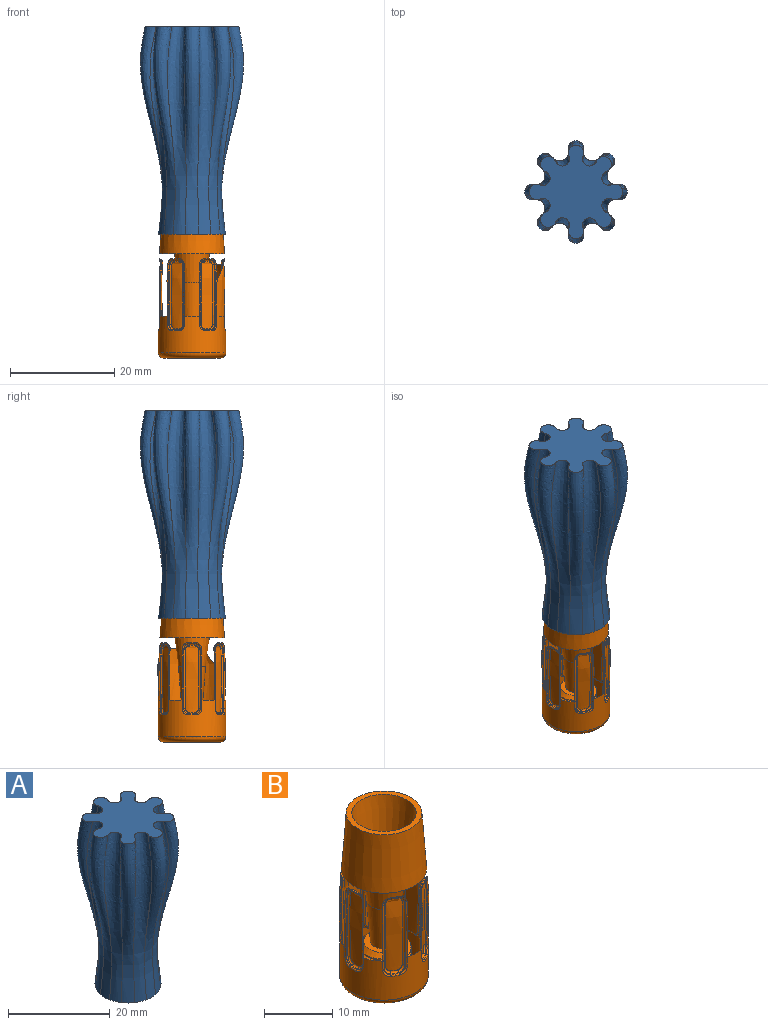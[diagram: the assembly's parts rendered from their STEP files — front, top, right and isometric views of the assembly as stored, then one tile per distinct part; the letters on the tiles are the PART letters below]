
ASSEMBLY  parts=2 mates=1
PART A: 18 faces, bbox 22.6x22.6x40 mm
  f0: plane 18x18mm, normal (0,0,1), area 169.5mm2, adj f2,f3,f4,f5,f6,f7,f8,f9
  f1: plane 13x13mm, normal (0,0,-1), area 132.7mm2, adj f2,f3,f4,f5,f6,f7,f8,f9
  f2: bspline ~40x5.48mm, area 140.4mm2, adj f0,f1,f3,f17
  f3: bspline ~40x5.84mm, area 146.5mm2, adj f0,f1,f2,f4
  f4: bspline ~40x5.48mm, area 140.4mm2, adj f0,f1,f3,f5
  f5: bspline ~40x6.75mm, area 146.5mm2, adj f0,f1,f4,f6
  f6: bspline ~40x5.48mm, area 140.4mm2, adj f0,f1,f5,f7
  f7: bspline ~40x5.84mm, area 146.5mm2, adj f0,f1,f6,f8
  f8: bspline ~40x5.48mm, area 140.4mm2, adj f0,f1,f7,f9
  f9: bspline ~40x6.75mm, area 146.5mm2, adj f0,f1,f8,f10
  f10: bspline ~40x5.48mm, area 140.4mm2, adj f0,f1,f9,f11
  f11: bspline ~40x5.84mm, area 146.5mm2, adj f0,f1,f10,f12
  f12: bspline ~40x5.48mm, area 140.4mm2, adj f0,f1,f11,f13
  f13: bspline ~40x6.75mm, area 146.5mm2, adj f0,f1,f12,f14
  f14: bspline ~40x5.48mm, area 140.4mm2, adj f0,f1,f13,f15
  f15: bspline ~40x5.84mm, area 146.5mm2, adj f0,f1,f14,f16
  f16: bspline ~40x5.48mm, area 140.4mm2, adj f0,f1,f15,f17
  f17: bspline ~40x6.75mm, area 146.5mm2, adj f0,f1,f2,f16
PART B: 180 faces, bbox 48.2x48.2x55.2 mm
  f0: plane 11x11mm, normal (0,0,-1), area 39.6mm2, adj f2,f177
  f1: cylinder r=6.5mm len=13mm, axis (0,0,-1), area 230.4mm2, adj f12,f37,f38,f39,f40,f41,f64,f65
  f2: cone r=4.2mm half-angle=45deg, axis (0,0,-1), area 18.5mm2, adj f0,f8,f9,f10,f11
  f3: plane 5.9x5.9mm, normal (0,0,-1), area 14.8mm2, adj f6,f179
  f4: plane 0.15x0.04mm, normal (-0.44,-0.9,0), area 0mm2, adj f5,f11
  f5: cylinder r=3.95mm len=3.48mm, axis (0,0,-1), area 0.3mm2, adj f4,f7,f10
  f6: cone r=2.95mm half-angle=45deg, axis (0,0,-1), area 19.2mm2, adj f3,f7,f9,f10
  f7: cone r=2.95mm half-angle=45deg, axis (0,0,-1), area 1.9mm2, adj f5,f6,f8,f10
  f8: bspline ~7.89x7.89mm, area 80.7mm2, adj f2,f7,f9,f11
  f9: cylinder r=3.43mm len=6.85mm, axis (0,0,1), area 30.4mm2, adj f2,f6,f8,f10
  f10: bspline ~7.9x7.89mm, area 80.6mm2, adj f2,f5,f6,f7,f9,f11
  f11: bspline ~9.25x8.32mm, area 24.8mm2, adj f2,f4,f8,f10
  f12: revolved ~13.14x13.13mm, area 207.3mm2, adj f1,f13,f32,f33,f34,f35,f36,f59
  f13: cone r=5.55mm half-angle=4deg, axis (0,0,-1), area 371.6mm2, adj f12,f14
  f14: plane 11.1x11.1mm, normal (0,0,1), area 27.4mm2, adj f13,f178
  f15: plane 1.29x0.23mm, normal (0,0,1), area 0.3mm2, adj f20,f23,f29,f41
  f16: cone r=8.65mm half-angle=83.7deg, axis (0,0,1), area 0.2mm2, adj f21,f22,f26,f32
  f17: plane 11.52x0.32mm, normal (0.26,0.97,0), area 1.5mm2, adj f22,f23,f25,f35,f37
  f18: plane 11.52x0.32mm, normal (0.26,-0.97,0), area 1.5mm2, adj f20,f21,f30,f36,f38
  f19: revolved ~12.85x2.53mm, area 31.3mm2, adj f24,f25,f26,f27,f28,f29,f30,f31
  f20: cylinder r=1mm len=1.04mm, axis (-0.97,-0.26,0), area 0.3mm2, adj f15,f18,f31,f40
  f21: bspline ~6.17x2.56mm, area 0.2mm2, adj f16,f18,f28,f34
  f22: bspline ~7.17x2.82mm, area 0.2mm2, adj f16,f17,f24,f33
  f23: cylinder r=1mm len=1.04mm, axis (0.97,-0.26,0), area 0.3mm2, adj f15,f17,f27,f39
  f24: bspline ~1.23x1.09mm, area 0.6mm2, adj f19,f22,f25,f26
  f25: bspline ~12.18x0.51mm, area 5.2mm2, adj f17,f19,f24,f27
  f26: torus R=5.99mm, axis (0,0,1), area 0.5mm2, adj f16,f19,f24,f28
  f27: bspline ~1.24x1.06mm, area 0.6mm2, adj f19,f23,f25,f29
  f28: bspline ~1.25x1.07mm, area 0.6mm2, adj f19,f21,f26,f30
  f29: torus R=6.09mm, axis (0,0,1), area 0.5mm2, adj f15,f19,f27,f31
  f30: bspline ~12.87x0.51mm, area 5.2mm2, adj f18,f19,f28,f31
  f31: bspline ~1.23x1.07mm, area 0.6mm2, adj f19,f20,f29,f30
  f32: torus R=6.11mm, axis (0,0,1), area 0.4mm2, adj f12,f16,f33,f34
  f33: bspline ~1.46x1.3mm, area 0.5mm2, adj f12,f22,f32,f35
  f34: bspline ~1.5x1.46mm, area 0.5mm2, adj f12,f21,f32,f36
  f35: bspline ~22.35x0.67mm, area 3.2mm2, adj f12,f17,f33,f37
  f36: bspline ~19.25x0.46mm, area 3.2mm2, adj f12,f18,f34,f38
  f37: cylinder r=0.2mm len=1.61mm, axis (0,0,-1), area 0.5mm2, adj f1,f17,f35,f39
  f38: cylinder r=0.2mm len=1.61mm, axis (0,0,-1), area 0.5mm2, adj f1,f18,f36,f40
  f39: bspline ~1.5x1.47mm, area 0.5mm2, adj f1,f23,f37,f41
  f40: bspline ~1.5x1.47mm, area 0.5mm2, adj f1,f20,f38,f41
  f41: torus R=6.3mm, axis (0,0,1), area 0.4mm2, adj f1,f15,f39,f40
  f42: plane 1.17x0.79mm, normal (0,0,1), area 0.3mm2, adj f47,f50,f56,f68
  f43: cone r=8.65mm half-angle=83.7deg, axis (0,0,1), area 0.2mm2, adj f48,f49,f53,f59
  f44: plane 11.52x0.32mm, normal (0.97,0.26,0), area 1.5mm2, adj f49,f50,f52,f62,f64
  f45: plane 11.52x0.23mm, normal (-0.71,-0.71,0), area 1.5mm2, adj f47,f48,f57,f63,f65
  f46: revolved ~12.85x2.27mm, area 31.3mm2, adj f51,f52,f53,f54,f55,f56,f57,f58
  f47: cylinder r=1mm len=1mm, axis (-0.71,0.71,0), area 0.3mm2, adj f42,f45,f58,f67
  f48: bspline ~5.1x5.03mm, area 0.2mm2, adj f43,f45,f55,f61
  f49: bspline ~7.28x2.81mm, area 0.2mm2, adj f43,f44,f51,f60
  f50: cylinder r=1mm len=1.04mm, axis (0.26,-0.97,0), area 0.3mm2, adj f42,f44,f54,f66
  f51: bspline ~1.23x1.03mm, area 0.6mm2, adj f46,f49,f52,f53
  f52: bspline ~12.87x0.6mm, area 5.2mm2, adj f44,f46,f51,f54
  f53: torus R=5.99mm, axis (0,0,1), area 0.5mm2, adj f43,f46,f51,f55
  f54: bspline ~1.23x1.06mm, area 0.6mm2, adj f46,f50,f52,f56
  f55: bspline ~1.19x1.07mm, area 0.6mm2, adj f46,f48,f53,f57
  f56: torus R=6.09mm, axis (0,0,1), area 0.5mm2, adj f42,f46,f54,f58
  f57: bspline ~12.87x0.58mm, area 5.2mm2, adj f45,f46,f55,f58
  f58: bspline ~1.23x1.12mm, area 0.6mm2, adj f46,f47,f56,f57
  f59: torus R=6.11mm, axis (0,0,1), area 0.4mm2, adj f12,f43,f60,f61
  f60: bspline ~1.46x1.2mm, area 0.5mm2, adj f12,f49,f59,f62
  f61: bspline ~1.46x1.28mm, area 0.5mm2, adj f12,f48,f59,f63
  f62: bspline ~22.35x0.71mm, area 3.2mm2, adj f12,f44,f60,f64
  f63: bspline ~19.25x0.48mm, area 3.2mm2, adj f12,f45,f61,f65
  f64: cylinder r=0.2mm len=1.61mm, axis (0,0,-1), area 0.5mm2, adj f1,f44,f62,f66
  f65: cylinder r=0.2mm len=1.61mm, axis (0,0,-1), area 0.5mm2, adj f1,f45,f63,f67
  f66: bspline ~1.47x1.43mm, area 0.5mm2, adj f1,f50,f64,f68
  f67: bspline ~1.47x1.24mm, area 0.5mm2, adj f1,f47,f65,f68
  f68: torus R=6.3mm, axis (0,0,1), area 0.4mm2, adj f1,f42,f66,f67
  f69: plane 1.17x0.79mm, normal (0,0,1), area 0.3mm2, adj f74,f77,f83,f95
  f70: cone r=8.65mm half-angle=83.7deg, axis (0,0,1), area 0.2mm2, adj f75,f76,f80,f86
  f71: plane 11.52x0.23mm, normal (0.71,-0.71,0), area 1.5mm2, adj f76,f77,f79,f89,f91
  f72: plane 11.52x0.32mm, normal (-0.97,0.26,0), area 1.5mm2, adj f74,f75,f84,f90,f92
  f73: revolved ~12.85x2.27mm, area 31.3mm2, adj f78,f79,f80,f81,f82,f83,f84,f85
  f74: cylinder r=1mm len=1.04mm, axis (0.26,0.97,0), area 0.3mm2, adj f69,f72,f85,f94
  f75: bspline ~6.28x2.54mm, area 0.2mm2, adj f70,f72,f82,f88
  f76: bspline ~5.83x5.76mm, area 0.2mm2, adj f70,f71,f78,f87
  f77: cylinder r=1mm len=1mm, axis (-0.71,-0.71,0), area 0.3mm2, adj f69,f71,f81,f93
  f78: bspline ~1.23x1.06mm, area 0.6mm2, adj f73,f76,f79,f80
  f79: bspline ~12.18x0.58mm, area 5.2mm2, adj f71,f73,f78,f81
  f80: torus R=5.99mm, axis (0,0,1), area 0.5mm2, adj f70,f73,f78,f82
  f81: bspline ~1.12x1.06mm, area 0.6mm2, adj f73,f77,f79,f83
  f82: bspline ~1.19x1.07mm, area 0.6mm2, adj f73,f75,f80,f84
  f83: torus R=6.09mm, axis (0,0,1), area 0.5mm2, adj f69,f73,f81,f85
  f84: bspline ~12.87x0.6mm, area 5.2mm2, adj f72,f73,f82,f85
  f85: bspline ~1.23x1.23mm, area 0.6mm2, adj f73,f74,f83,f84
  f86: torus R=6.11mm, axis (0,0,1), area 0.4mm2, adj f12,f70,f87,f88
  f87: bspline ~1.28x1.26mm, area 0.5mm2, adj f12,f76,f86,f89
  f88: bspline ~1.46x1.39mm, area 0.5mm2, adj f12,f75,f86,f90
  f89: bspline ~22.35x0.63mm, area 3.2mm2, adj f12,f71,f87,f91
  f90: bspline ~19.25x0.5mm, area 3.2mm2, adj f12,f72,f88,f92
  f91: cylinder r=0.2mm len=1.61mm, axis (0,0,-1), area 0.5mm2, adj f1,f71,f89,f93
  f92: cylinder r=0.2mm len=1.61mm, axis (0,0,-1), area 0.5mm2, adj f1,f72,f90,f94
  f93: bspline ~1.47x1.24mm, area 0.5mm2, adj f1,f77,f91,f95
  f94: bspline ~1.47x1.43mm, area 0.5mm2, adj f1,f74,f92,f95
  f95: torus R=6.3mm, axis (0,0,1), area 0.4mm2, adj f1,f69,f93,f94
  f96: plane 1.29x0.23mm, normal (0,0,1), area 0.3mm2, adj f101,f104,f110,f122
  f97: cone r=8.65mm half-angle=83.7deg, axis (0,0,1), area 0.2mm2, adj f102,f103,f107,f113
  f98: plane 11.52x0.32mm, normal (-0.26,-0.97,0), area 1.5mm2, adj f103,f104,f106,f116,f118
  f99: plane 11.52x0.32mm, normal (-0.26,0.97,0), area 1.5mm2, adj f101,f102,f111,f117,f119
  f100: revolved ~12.85x2.53mm, area 31.3mm2, adj f105,f106,f107,f108,f109,f110,f111,f112
  f101: cylinder r=1mm len=1.04mm, axis (0.97,0.26,0), area 0.3mm2, adj f96,f99,f112,f121
  f102: bspline ~6.17x2.56mm, area 0.2mm2, adj f97,f99,f109,f115
  f103: bspline ~7.17x2.82mm, area 0.2mm2, adj f97,f98,f105,f114
  f104: cylinder r=1mm len=1.04mm, axis (-0.97,0.26,0), area 0.3mm2, adj f96,f98,f108,f120
  f105: bspline ~1.23x1.09mm, area 0.6mm2, adj f100,f103,f106,f107
  f106: bspline ~12.18x0.51mm, area 5.2mm2, adj f98,f100,f105,f108
  f107: torus R=5.99mm, axis (0,0,1), area 0.5mm2, adj f97,f100,f105,f109
  f108: bspline ~1.24x1.06mm, area 0.6mm2, adj f100,f104,f106,f110
  f109: bspline ~1.25x1.07mm, area 0.6mm2, adj f100,f102,f107,f111
  f110: torus R=6.09mm, axis (0,0,1), area 0.5mm2, adj f96,f100,f108,f112
  f111: bspline ~12.87x0.51mm, area 5.2mm2, adj f99,f100,f109,f112
  f112: bspline ~1.24x1.23mm, area 0.6mm2, adj f100,f101,f110,f111
  f113: torus R=6.11mm, axis (0,0,1), area 0.4mm2, adj f12,f97,f114,f115
  f114: bspline ~1.46x1.3mm, area 0.5mm2, adj f12,f103,f113,f116
  f115: bspline ~1.5x1.46mm, area 0.5mm2, adj f12,f102,f113,f117
  f116: bspline ~22.35x0.67mm, area 3.2mm2, adj f12,f98,f114,f118
  f117: bspline ~19.25x0.46mm, area 3.2mm2, adj f12,f99,f115,f119
  f118: cylinder r=0.2mm len=1.61mm, axis (0,0,-1), area 0.5mm2, adj f1,f98,f116,f120
  f119: cylinder r=0.2mm len=1.61mm, axis (0,0,-1), area 0.5mm2, adj f1,f99,f117,f121
  f120: bspline ~1.5x1.47mm, area 0.5mm2, adj f1,f104,f118,f122
  f121: bspline ~1.5x1.47mm, area 0.5mm2, adj f1,f101,f119,f122
  f122: torus R=6.3mm, axis (0,0,1), area 0.4mm2, adj f1,f96,f120,f121
  f123: plane 1.17x0.79mm, normal (0,0,1), area 0.3mm2, adj f128,f131,f137,f149
  f124: cone r=8.65mm half-angle=83.7deg, axis (0,0,1), area 0.2mm2, adj f129,f130,f134,f140
  f125: plane 11.52x0.32mm, normal (-0.97,-0.26,0), area 1.5mm2, adj f130,f131,f133,f143,f145
  f126: plane 11.52x0.23mm, normal (0.71,0.71,0), area 1.5mm2, adj f128,f129,f138,f144,f146
  f127: revolved ~12.85x2.27mm, area 31.3mm2, adj f132,f133,f134,f135,f136,f137,f138,f139
  f128: cylinder r=1mm len=1mm, axis (0.71,-0.71,0), area 0.3mm2, adj f123,f126,f139,f148
  f129: bspline ~5.1x5.03mm, area 0.2mm2, adj f124,f126,f136,f142
  f130: bspline ~7.28x2.81mm, area 0.2mm2, adj f124,f125,f132,f141
  f131: cylinder r=1mm len=1.04mm, axis (-0.26,0.97,0), area 0.3mm2, adj f123,f125,f135,f147
  f132: bspline ~1.23x1.03mm, area 0.6mm2, adj f127,f130,f133,f134
  f133: bspline ~12.18x0.6mm, area 5.2mm2, adj f125,f127,f132,f135
  f134: torus R=5.99mm, axis (0,0,1), area 0.5mm2, adj f124,f127,f132,f136
  f135: bspline ~1.23x1.06mm, area 0.6mm2, adj f127,f131,f133,f137
  f136: bspline ~1.19x1.07mm, area 0.6mm2, adj f127,f129,f134,f138
  f137: torus R=6.09mm, axis (0,0,1), area 0.5mm2, adj f123,f127,f135,f139
  f138: bspline ~12.87x0.58mm, area 5.2mm2, adj f126,f127,f136,f139
  f139: bspline ~1.23x1.12mm, area 0.6mm2, adj f127,f128,f137,f138
  f140: torus R=6.11mm, axis (0,0,1), area 0.4mm2, adj f12,f124,f141,f142
  f141: bspline ~1.46x1.2mm, area 0.5mm2, adj f12,f130,f140,f143
  f142: bspline ~1.46x1.28mm, area 0.5mm2, adj f12,f129,f140,f144
  f143: bspline ~22.35x0.71mm, area 3.2mm2, adj f12,f125,f141,f145
  f144: bspline ~19.25x0.48mm, area 3.2mm2, adj f12,f126,f142,f146
  f145: cylinder r=0.2mm len=1.61mm, axis (0,0,-1), area 0.5mm2, adj f1,f125,f143,f147
  f146: cylinder r=0.2mm len=1.61mm, axis (0,0,-1), area 0.5mm2, adj f1,f126,f144,f148
  f147: bspline ~1.47x1.43mm, area 0.5mm2, adj f1,f131,f145,f149
  f148: bspline ~1.47x1.24mm, area 0.5mm2, adj f1,f128,f146,f149
  f149: torus R=6.3mm, axis (0,0,1), area 0.4mm2, adj f1,f123,f147,f148
  f150: plane 1.17x0.79mm, normal (0,0,1), area 0.3mm2, adj f155,f158,f164,f176
  f151: cone r=8.65mm half-angle=83.7deg, axis (0,0,1), area 0.2mm2, adj f156,f157,f161,f167
  f152: plane 11.52x0.23mm, normal (-0.71,0.71,0), area 1.5mm2, adj f157,f158,f160,f170,f172
  f153: plane 11.52x0.32mm, normal (0.97,-0.26,0), area 1.5mm2, adj f155,f156,f165,f171,f173
  f154: revolved ~12.85x2.27mm, area 31.3mm2, adj f159,f160,f161,f162,f163,f164,f165,f166
  f155: cylinder r=1mm len=1.04mm, axis (-0.26,-0.97,0), area 0.3mm2, adj f150,f153,f166,f175
  f156: bspline ~6.28x2.54mm, area 0.2mm2, adj f151,f153,f163,f169
  f157: bspline ~5.83x5.76mm, area 0.2mm2, adj f151,f152,f159,f168
  f158: cylinder r=1mm len=1mm, axis (0.71,0.71,0), area 0.3mm2, adj f150,f152,f162,f174
  f159: bspline ~1.23x1.06mm, area 0.6mm2, adj f154,f157,f160,f161
  f160: bspline ~12.18x0.58mm, area 5.2mm2, adj f152,f154,f159,f162
  f161: torus R=5.99mm, axis (0,0,1), area 0.5mm2, adj f151,f154,f159,f163
  f162: bspline ~1.12x1.06mm, area 0.6mm2, adj f154,f158,f160,f164
  f163: bspline ~1.19x1.07mm, area 0.6mm2, adj f154,f156,f161,f165
  f164: torus R=6.09mm, axis (0,0,1), area 0.5mm2, adj f150,f154,f162,f166
  f165: bspline ~12.87x0.6mm, area 5.2mm2, adj f153,f154,f163,f166
  f166: bspline ~1.23x1.23mm, area 0.6mm2, adj f154,f155,f164,f165
  f167: torus R=6.11mm, axis (0,0,1), area 0.4mm2, adj f12,f151,f168,f169
  f168: bspline ~1.46x1.13mm, area 0.5mm2, adj f12,f157,f167,f170
  f169: bspline ~1.46x1.39mm, area 0.5mm2, adj f12,f156,f167,f171
  f170: bspline ~22.35x0.63mm, area 3.2mm2, adj f12,f152,f168,f172
  f171: bspline ~19.25x0.5mm, area 3.2mm2, adj f12,f153,f169,f173
  f172: cylinder r=0.2mm len=1.61mm, axis (0,0,-1), area 0.5mm2, adj f1,f152,f170,f174
  f173: cylinder r=0.2mm len=1.61mm, axis (0,0,-1), area 0.5mm2, adj f1,f153,f171,f175
  f174: bspline ~1.47x1.24mm, area 0.5mm2, adj f1,f158,f172,f176
  f175: bspline ~1.47x1.43mm, area 0.5mm2, adj f1,f155,f173,f176
  f176: torus R=6.3mm, axis (0,0,1), area 0.4mm2, adj f1,f150,f174,f175
  f177: torus R=5.5mm, axis (0,0,1), area 60.6mm2, adj f0,f1
  f178: cone r=4.7mm half-angle=7.7deg, axis (0,0,1), area 359.5mm2, adj f14,f179
  f179: torus R=71.97mm, axis (0,0,-1), area 105.3mm2, adj f3,f178
PLACE A t=(-9.81,22.07,20.61)mm
PLACE B t=(-9.81,22.07,-3.15)mm
MATE slider B.f2 <-> A.f1  axis (0,0,-1) through (-9.81,22.07,21.85)mm
